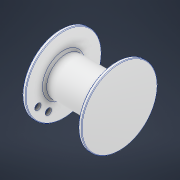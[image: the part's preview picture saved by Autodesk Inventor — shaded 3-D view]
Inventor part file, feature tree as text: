
AUTODESK INVENTOR PART (.ipt)
format: ipt  version: 2021 (Build 250183000, 183)  size: 193,536 bytes
history: native  units: mm
features: sketch x3, fillet x2, revolve x1, hole x1, extrude x1, chamfer x1
ambient origin geometry x8: Origin, YZ Plane, XZ Plane, XY Plane, X Axis, Y Axis, Z Axis, Center Point
bodies: Solid1 (feature_tree)
feature tree (9):
  revolve  "Revolution1"  [1 undecoded]
  hole  "Hole1"  [1 undecoded]
  extrude  "Extrusion1"  Depth=0.5mm
  chamfer  "Chamfer1"  Distance=3.0mm
  fillet  "Fillet1"  Radius=1.3mm
  fillet  "Fillet2"  Radius=22.0mm
  sketch  "Sketch1"  dims[d0=3.0mm d1=18.0mm]
  sketch  "Sketch2"  dims[d2=36.0mm d3=25.0mm]
  sketch  "Sketch3"  dims[d4=90.0deg d5=6.0mm d6=6.0mm d7=4.0mm d8=2.0mm d9=90.0deg d10=8.0mm d11=20.594885mm d12=7.0mm d13=3.0mm d14=1.3mm d15=22.0mm d16=0.0mm d17=0.5mm d18=2.0mm d19=45.0deg d20=2.0mm d21=0.5mm]
note: 2 required parameter values undecoded (feature->parameter linkage not recoverable at this tier; creation-order binding heuristic only, values carry confidence <= 0.55)